# Revit family: SNS Merlin Liquid Petroleum Gas Detector TFT
name_source: partatom
category: Electrical Equipment
units: mm (PartAtom-declared; Revit-internal decimal feet)

## family parameters
Always vertical = Yes
Cut with Voids When Loaded = No
OmniClass Number = 23.80.30.11.17
OmniClass Title = Distribution Boards and Control Panels
Part Type = Other Panel
Room Calculation Point = No
Round Connector Dimension = Use Diameter
Shared = No
Work Plane-Based = No

## types (1)
- SNS Merlin LPG TFT Gas Detector
    Default Height = 4' - 0"
    Description = The TFT range of SNS detectors work in combination with the SNS Merlin range of Gas Detection panels and Utility Controllers. Semi conductor type sensor for industrial and commercial indoor applications. Compact, modern, digital design makes the units aesthetically pleasing and easy to install.

The LPG sensor should be mounted in accordance with certain considerations. Do not position next to burners, heaters or ovens where temperatures above the room ambient may be experienced. It is, if possible, better to mount the sensors on the opposite wall. This is, of course, dependant on the size of the protected area. LPG is heavier than air and will therefore drop, meaning the Gas sensor should be mounted 10 inches from the floor of the protected area. The LPG detectors at detection will go into alarm at 10% of the low explosion level. This will trigger isolation of the power supply to the solenoid and as such isolation of the gas supply. This can then be rectified by resolving the leak, allowing the sensor head to clear and resetting the attached Merlin panel.
    Load = 120 VA
    Manufacturer = S&S Northern Ltd.
    Model = SNS Merlin LPG TFT Gas Detector
    Product Information = https://snsnorthern.com
    Type Comments = The TFT range of SNS detectors work in combination with the SNS Merlin range of Gas Detection panels and Utility Controllers. Semi conductor type sensor for industrial and commercial indoor applications. Compact, modern, digital design makes the units aesthetically pleasing and easy to install.

The LPG sensor should be mounted in accordance with certain considerations. Do not position next to burners, heaters or ovens where temperatures above the room ambient may be experienced. It is, if possible, better to mount the sensors on the opposite wall. This is, of course, dependant on the size of the protected area. LPG is heavier than air and will therefore drop, meaning the Gas sensor should be mounted 10 inches from the floor of the protected area. The LPG detectors at detection will go into alarm at 10% of the low explosion level. This will trigger isolation of the power supply to the solenoid and as such isolation of the gas supply. This can then be rectified by resolving the leak, allowing the sensor head to clear and resetting the attached Merlin panel.
    URL = https://snsnorthern.com
    Voltage = 120VAC

## geometry (parser evidence)
native form markers: Sweep x17
no freeform markers — native parametric forms only
